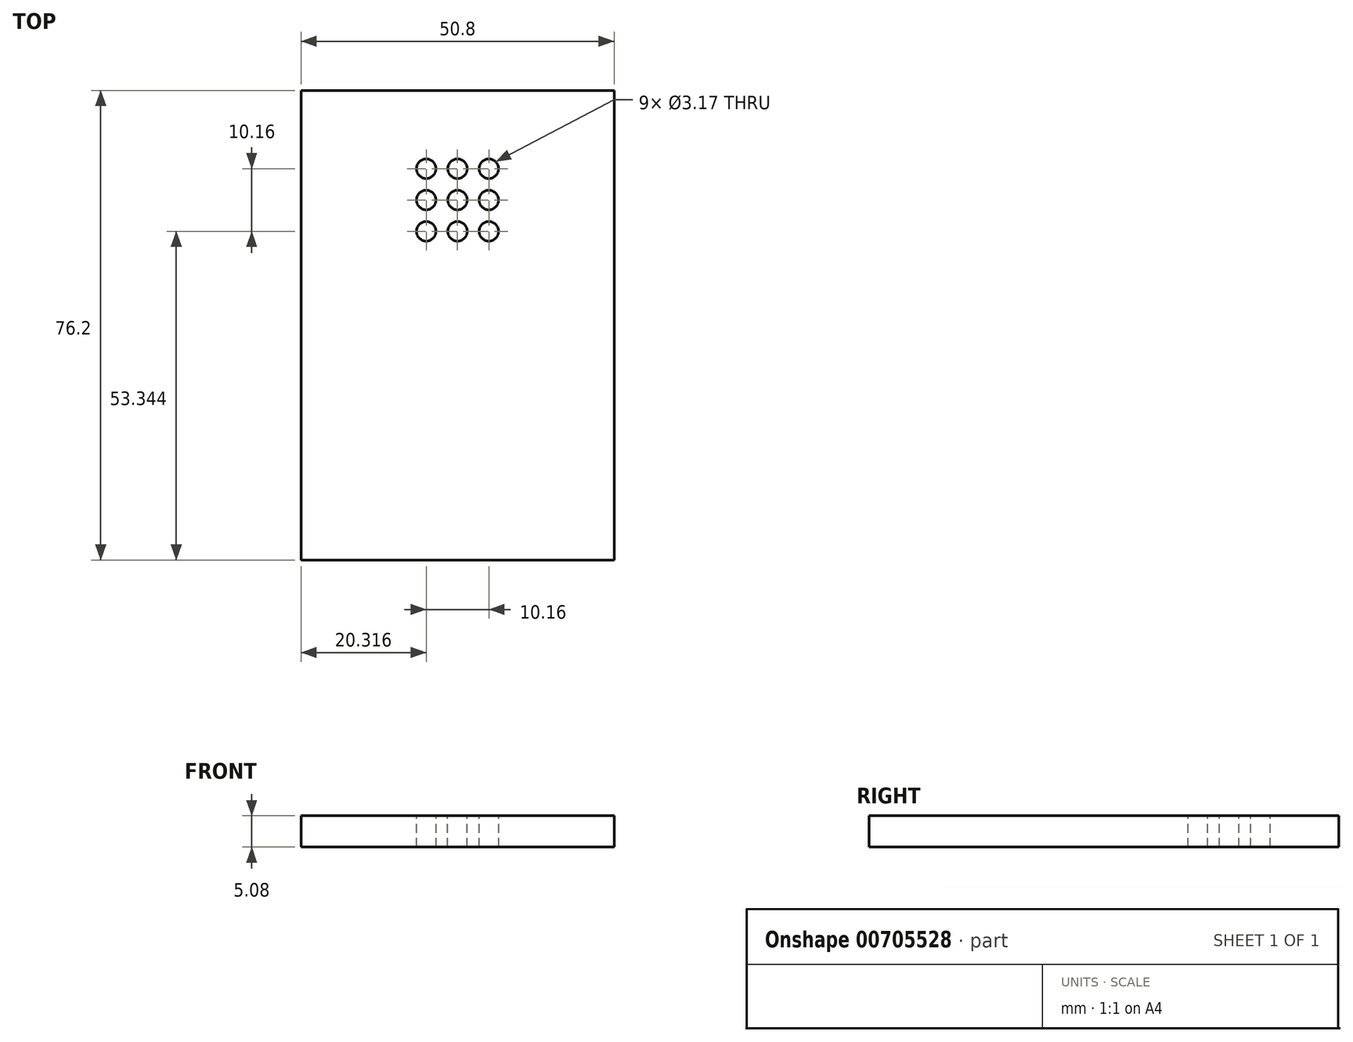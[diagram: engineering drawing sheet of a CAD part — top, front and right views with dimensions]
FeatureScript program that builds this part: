
annotation { "Feature Type Name" : "Feature", "Feature Type Description" : "" }
export const myFeature = defineFeature(function(context is Context, id is Id, definition is map)
    precondition{}
    {
        {
            var Q0;
            Q0=qCreatedBy(makeId("Top.planeOp"),FACE);
            var sketch = newSketch(context, id + "F0", { "sketchPlane" : qUnion([Q0])});
            skLineSegment(sketch, "E0.bottom", {"start": v(-39.4, 21.67) * mm, "end": v(11.4, 21.67) * mm});
            skLineSegment(sketch, "E0.top", {"start": v(-39.4, -54.53) * mm, "end": v(11.4, -54.53) * mm});
            skLineSegment(sketch, "E0.left", {"start": v(-39.4, 21.67) * mm, "end": v(-39.4, -54.53) * mm});
            skLineSegment(sketch, "E0.right", {"start": v(11.4, 21.67) * mm, "end": v(11.4, -54.53) * mm});
            skSolve(sketch);
        }
        {
            var Q0;
            Q0=makeQuery(id+"F0.imprint","IMPRINT",FACE,{"disambiguationData":[TD([[makeQuery(id+"F0.imprint","IMPRINT",EDGE,{"derivedFrom":sQuery(id+"F0.wireOp",EDGE,"E0.bottom")}),-1.0]])]});
            extrude(context, id + "F1", {"entities" : qUnion([Q0]), "depth" : 5.08 * mm, "offsetDistance" : 25.4 * mm});
        }
        {
            var Q0;
            Q0=makeQuery(id+"F1.opExtrude","CAP_FACE",FACE,{"disambiguationData":[OSD([sQuery(id+"F0.wireOp",EDGE,"E0.bottom"),sQuery(id+"F0.wireOp",EDGE,"E0.top"),sQuery(id+"F0.wireOp",EDGE,"E0.left"),sQuery(id+"F0.wireOp",EDGE,"E0.right")])],"isStart":false});
            var sketch = newSketch(context, id + "F2", { "sketchPlane" : qUnion([Q0])});
            skCircle(sketch, "E1", {"center": v(-19.08, 8.97) * mm, "radius": 1.59 * mm});
            skCircle(sketch, "E2", {"center": v(-14, 8.97) * mm, "radius": 1.59 * mm});
            skCircle(sketch, "E3", {"center": v(-8.92, 8.97) * mm, "radius": 1.59 * mm});
            skCircle(sketch, "E4", {"center": v(-19.08, 3.9) * mm, "radius": 1.59 * mm});
            skCircle(sketch, "E5", {"center": v(-14, 3.9) * mm, "radius": 1.59 * mm});
            skCircle(sketch, "E6", {"center": v(-8.92, 3.9) * mm, "radius": 1.59 * mm});
            skCircle(sketch, "E7", {"center": v(-19.08, -1.19) * mm, "radius": 1.59 * mm});
            skCircle(sketch, "E8", {"center": v(-14, -1.19) * mm, "radius": 1.59 * mm});
            skCircle(sketch, "E9", {"center": v(-8.92, -1.19) * mm, "radius": 1.59 * mm});
            skSolve(sketch);
        }
        {
            var Q0;
            Q0=makeQuery(id+"F2.imprint","IMPRINT",FACE,{"disambiguationData":[TD([[makeQuery(id+"F2.imprint","IMPRINT",EDGE,{"derivedFrom":sQuery(id+"F2.wireOp",EDGE,"E1")}),1.0]])]});
            var Q1;
            Q1=makeQuery(id+"F2.imprint","IMPRINT",FACE,{"disambiguationData":[TD([[makeQuery(id+"F2.imprint","IMPRINT",EDGE,{"derivedFrom":sQuery(id+"F2.wireOp",EDGE,"E2")}),1.0]])]});
            var Q2;
            Q2=makeQuery(id+"F2.imprint","IMPRINT",FACE,{"disambiguationData":[TD([[makeQuery(id+"F2.imprint","IMPRINT",EDGE,{"derivedFrom":sQuery(id+"F2.wireOp",EDGE,"E3")}),1.0]])]});
            var Q3;
            Q3=makeQuery(id+"F2.imprint","IMPRINT",FACE,{"disambiguationData":[TD([[makeQuery(id+"F2.imprint","IMPRINT",EDGE,{"derivedFrom":sQuery(id+"F2.wireOp",EDGE,"E4")}),1.0]])]});
            var Q4;
            Q4=makeQuery(id+"F2.imprint","IMPRINT",FACE,{"disambiguationData":[TD([[makeQuery(id+"F2.imprint","IMPRINT",EDGE,{"derivedFrom":sQuery(id+"F2.wireOp",EDGE,"E5")}),1.0]])]});
            var Q5;
            Q5=makeQuery(id+"F2.imprint","IMPRINT",FACE,{"disambiguationData":[TD([[makeQuery(id+"F2.imprint","IMPRINT",EDGE,{"derivedFrom":sQuery(id+"F2.wireOp",EDGE,"E6")}),1.0]])]});
            var Q6;
            Q6=makeQuery(id+"F2.imprint","IMPRINT",FACE,{"disambiguationData":[TD([[makeQuery(id+"F2.imprint","IMPRINT",EDGE,{"derivedFrom":sQuery(id+"F2.wireOp",EDGE,"E7")}),1.0]])]});
            var Q7;
            Q7=makeQuery(id+"F2.imprint","IMPRINT",FACE,{"disambiguationData":[TD([[makeQuery(id+"F2.imprint","IMPRINT",EDGE,{"derivedFrom":sQuery(id+"F2.wireOp",EDGE,"E8")}),1.0]])]});
            var Q8;
            Q8=makeQuery(id+"F2.imprint","IMPRINT",FACE,{"disambiguationData":[TD([[makeQuery(id+"F2.imprint","IMPRINT",EDGE,{"derivedFrom":sQuery(id+"F2.wireOp",EDGE,"E9")}),1.0]])]});
            var Q9;
            Q9=makeQuery(id+"F2.imprint","IMPRINT",FACE,{"disambiguationData":[TD([[makeQuery(id+"F2.imprint","IMPRINT",EDGE,{"derivedFrom":sQuery(id+"F2.wireOp",EDGE,"zo5HgFdr-x02T-MjzD-2sJO-lCkmcUXBmvrX")}),1.0]])]});
            extrude(context, id + "F3", {"entities" : qUnion([Q0, Q1, Q2, Q3, Q4, Q5, Q6, Q7, Q8, Q9]), "operationType" : NewBodyOperationType.REMOVE, "oppositeDirection" : true, "depth" : 76.2 * mm, "offsetDistance" : 25.4 * mm});
        }
    });
